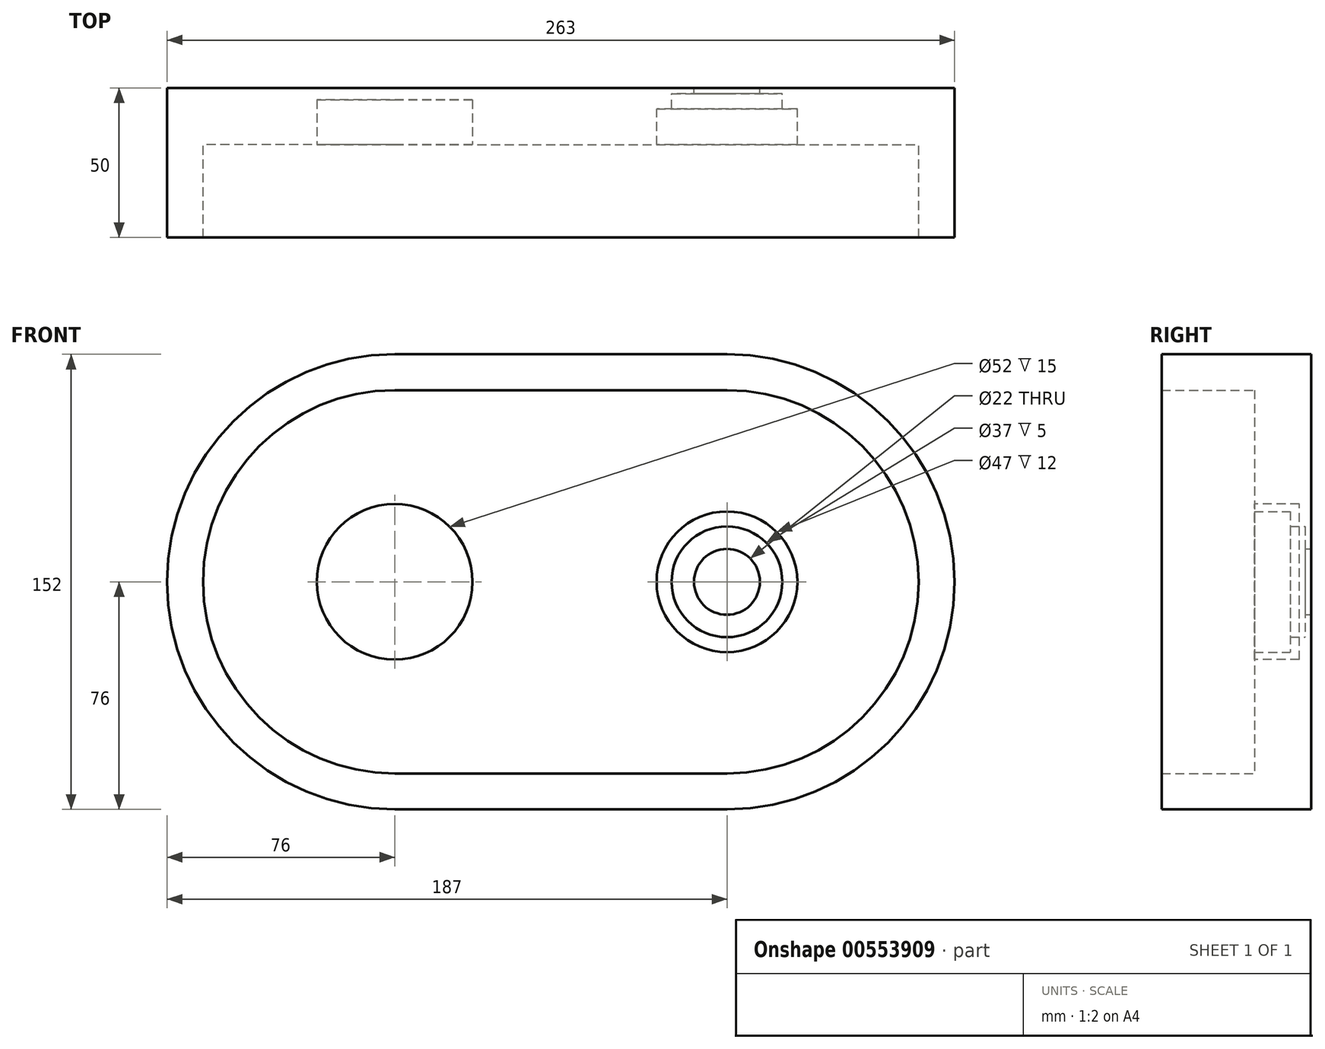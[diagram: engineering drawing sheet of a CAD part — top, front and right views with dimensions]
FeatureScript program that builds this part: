
annotation { "Feature Type Name" : "Feature", "Feature Type Description" : "" }
export const myFeature = defineFeature(function(context is Context, id is Id, definition is map)
    precondition{}
    {
        {
            var Q0;
            Q0=qCreatedBy(makeId("Front.planeOp"),FACE);
            var sketch = newSketch(context, id + "F0", { "sketchPlane" : qUnion([Q0])});
            skLineSegment(sketch, "E0.bottom", {"start": v(55.5, -76) * mm, "end": v(-55.5, -76) * mm});
            skLineSegment(sketch, "E0.top", {"start": v(55.5, 76) * mm, "end": v(-55.5, 76) * mm});
            skPoint(sketch, "E0.middle", {"position": v(0, 0) * mm});
            skArc(sketch, "E1", {"start": v(-55.5, 76) * mm, "mid": v(-131.5, 0) * mm, "end": v(-55.5, -76) * mm});
            skArc(sketch, "E2", {"start": v(55.5, -76) * mm, "mid": v(131.5, 0) * mm, "end": v(55.5, 76) * mm});
            skArc(sketch, "E3", {"start": v(-55.5, 64) * mm, "mid": v(-119.5, 0) * mm, "end": v(-55.5, -64) * mm});
            skArc(sketch, "E4", {"start": v(55.5, -64) * mm, "mid": v(119.5, 0) * mm, "end": v(55.5, 64) * mm});
            skLineSegment(sketch, "E5", {"start": v(-55.5, -64) * mm, "end": v(-55.5, 64) * mm, "construction": true});
            skLineSegment(sketch, "E6", {"start": v(55.5, -64) * mm, "end": v(55.5, 64) * mm, "construction": true});
            skLineSegment(sketch, "E7", {"start": v(-55.5, 64) * mm, "end": v(55.5, 64) * mm});
            skLineSegment(sketch, "E8", {"start": v(-55.5, -64) * mm, "end": v(55.5, -64) * mm});
            skSolve(sketch);
        }
        {
            var Q0;
            Q0 = qSketchRegion(id + "F0", true);
            extrude(context, id + "F1", {"entities" : qUnion([Q0]), "depth" : 50 * mm, "offsetDistance" : 25 * mm});
        }
        {
            var Q0;
            Q0=makeQuery(id+"F0.imprint","IMPRINT",FACE,{"disambiguationData":[TD([[makeQuery(id+"F0.imprint","IMPRINT",EDGE,{"derivedFrom":sQuery(id+"F0.wireOp",EDGE,"E3")}),1.0]])]});
            extrude(context, id + "F2", {"entities" : qUnion([Q0]), "operationType" : NewBodyOperationType.ADD, "depth" : 19 * mm, "offsetDistance" : 25 * mm});
        }
        {
            var Q0;
            Q0=makeQuery(id+"F2.opExtrude","CAP_FACE",FACE,{"disambiguationData":[OSD([sQuery(id+"F0.wireOp",EDGE,"E3"),sQuery(id+"F0.wireOp",EDGE,"E4"),sQuery(id+"F0.wireOp",EDGE,"E7"),sQuery(id+"F0.wireOp",EDGE,"E8")])],"isStart":false});
            var sketch = newSketch(context, id + "F3", { "sketchPlane" : qUnion([Q0])});
            skLineSegment(sketch, "E9", {"start": v(-55.5, 0) * mm, "end": v(55.5, 0) * mm, "construction": true});
            skCircle(sketch, "E10", {"center": v(-55.5, 0) * mm, "radius": 26 * mm});
            skSolve(sketch);
        }
        {
            var Q0;
            Q0 = qSketchRegion(id + "F3", true);
            extrude(context, id + "F4", {"entities" : qUnion([Q0]), "operationType" : NewBodyOperationType.REMOVE, "oppositeDirection" : true, "depth" : 15 * mm, "offsetDistance" : 25 * mm});
        }
        {
            var Q0;
            Q0=qCreatedBy(makeId("Right.planeOp"),FACE);
            cPlane(context, id + "F5", {"entities" : qUnion([Q0]), "cplaneType" : CPlaneType.OFFSET, "offset" : 55.5 * mm, "width" : 150 * mm, "height" : 150 * mm});
        }
        {
            var Q0;
            Q0=qCreatedBy(id+"F5.planeOp",FACE);
            var sketch = newSketch(context, id + "F6", { "sketchPlane" : qUnion([Q0])});
            skLineSegment(sketch, "E11", {"start": v(0, 0) * mm, "end": v(-46.35, 0) * mm, "construction": true});
            skLineSegment(sketch, "E12", {"start": v(0, 11) * mm, "end": v(-2, 11) * mm});
            skLineSegment(sketch, "E13", {"start": v(-2, 11) * mm, "end": v(-2, 18.5) * mm});
            skLineSegment(sketch, "E14", {"start": v(-2, 18.5) * mm, "end": v(-7, 18.5) * mm});
            skLineSegment(sketch, "E15", {"start": v(-7, 18.5) * mm, "end": v(-7, 23.5) * mm});
            skLineSegment(sketch, "E16", {"start": v(-7, 23.5) * mm, "end": v(-19, 23.5) * mm});
            skLineSegment(sketch, "E17", {"start": v(-19, 23.5) * mm, "end": v(-19, 0) * mm});
            skLineSegment(sketch, "E18", {"start": v(0, 11) * mm, "end": v(0, 0) * mm});
            skLineSegment(sketch, "E19", {"start": v(-19, 0) * mm, "end": v(0, 0) * mm});
            skSolve(sketch);
        }
        {
            var Q0;
            Q0 = qSketchRegion(id + "F6", true);
            var Q1;
            Q1=sQuery(id+"F6.wireOp",EDGE,"E19");
            revolve(context, id + "F7", {"operationType" : NewBodyOperationType.REMOVE, "entities" : qUnion([Q0]), "axis" : qUnion([Q1]), "revolveType" : RevolveType.FULL, "oppositeDirection" : true});
        }
    });
